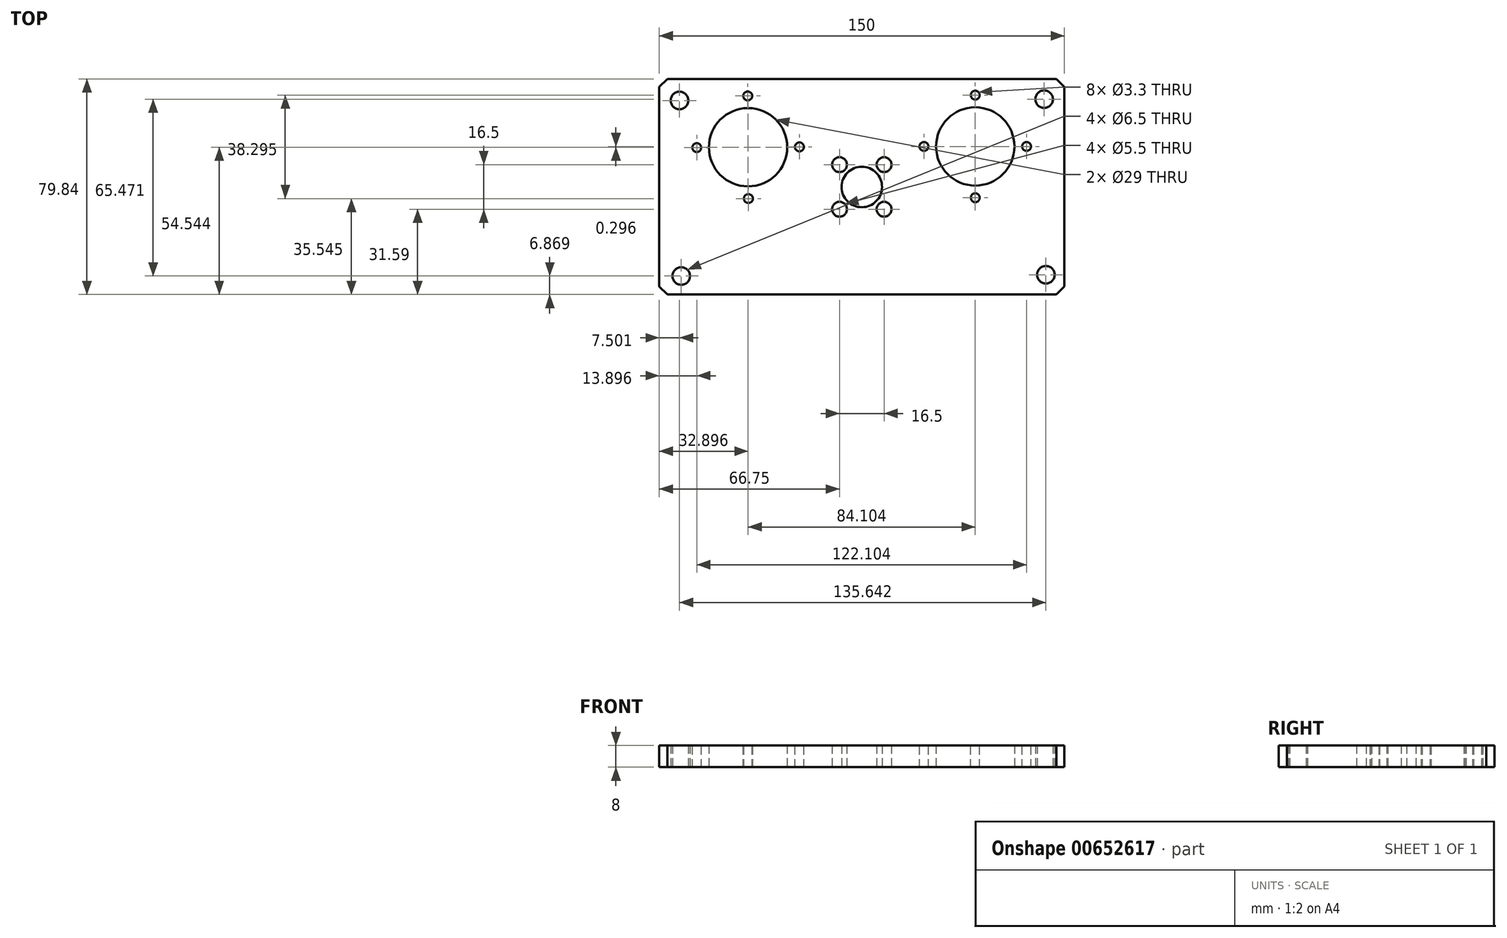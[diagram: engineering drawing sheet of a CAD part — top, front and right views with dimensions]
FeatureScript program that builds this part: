
annotation { "Feature Type Name" : "Feature", "Feature Type Description" : "" }
export const myFeature = defineFeature(function(context is Context, id is Id, definition is map)
    precondition{}
    {
        {
            var Q0;
            Q0=qCreatedBy(makeId("Top.planeOp"),FACE);
            var sketch = newSketch(context, id + "F0", { "sketchPlane" : qUnion([Q0])});
            skLineSegment(sketch, "E0.bottom", {"start": v(-75, 40) * mm, "end": v(75, 40) * mm});
            skLineSegment(sketch, "E0.top", {"start": v(-75, -39.84) * mm, "end": v(75, -39.84) * mm});
            skLineSegment(sketch, "E0.left", {"start": v(-75, 40) * mm, "end": v(-75, -39.84) * mm});
            skLineSegment(sketch, "E0.right", {"start": v(75, 40) * mm, "end": v(75, -39.84) * mm});
            skCircle(sketch, "E1", {"center": v(67.5, 32.5) * mm, "radius": 3.25 * mm});
            skCircle(sketch, "E2.0.1.0", {"center": v(68.14, -32.5) * mm, "radius": 3.25 * mm});
            skCircle(sketch, "E2.1.0.0", {"center": v(-67.5, 32.03) * mm, "radius": 3.25 * mm});
            skCircle(sketch, "E2.1.1.0", {"center": v(-66.86, -32.97) * mm, "radius": 3.25 * mm});
            skLineSegment(sketch, "E2.direction1", {"start": v(67.5, 32.5) * mm, "end": v(-67.5, 32.03) * mm, "construction": true});
            skLineSegment(sketch, "E2.direction2", {"start": v(67.5, 32.5) * mm, "end": v(68.14, -32.5) * mm, "construction": true});
            skCircle(sketch, "E3", {"center": v(0, 0) * mm, "radius": 7.5 * mm});
            skLineSegment(sketch, "E4.bottom", {"start": v(-8.25, 8.25) * mm, "end": v(8.25, 8.25) * mm, "construction": true});
            skLineSegment(sketch, "E4.top", {"start": v(-8.25, -8.25) * mm, "end": v(8.25, -8.25) * mm, "construction": true});
            skLineSegment(sketch, "E4.left", {"start": v(-8.25, 8.25) * mm, "end": v(-8.25, -8.25) * mm, "construction": true});
            skLineSegment(sketch, "E4.right", {"start": v(8.25, 8.25) * mm, "end": v(8.25, -8.25) * mm, "construction": true});
            skCircle(sketch, "E5", {"center": v(-8.25, 8.25) * mm, "radius": 2.75 * mm});
            skCircle(sketch, "E6.1.0", {"center": v(-8.25, -8.25) * mm, "radius": 2.75 * mm});
            skCircle(sketch, "E6.2.0", {"center": v(8.25, -8.25) * mm, "radius": 2.75 * mm});
            skCircle(sketch, "E6.3.0", {"center": v(8.25, 8.25) * mm, "radius": 2.75 * mm});
            skCircle(sketch, "E7", {"center": v(42, 15) * mm, "radius": 14.5 * mm});
            skCircle(sketch, "E8", {"center": v(23, 15) * mm, "radius": 1 * mm});
            skLineSegment(sketch, "E9", {"start": v(42, 15) * mm, "end": v(23, 15) * mm, "construction": true});
            skCircle(sketch, "E10.1.0", {"center": v(42, -4) * mm, "radius": 1 * mm});
            skCircle(sketch, "E10.2.0", {"center": v(61, 15) * mm, "radius": 1 * mm});
            skCircle(sketch, "E10.3.0", {"center": v(42, 34) * mm, "radius": 1 * mm});
            skLineSegment(sketch, "E11", {"start": v(0, 0) * mm, "end": v(-0.19, 53.35) * mm, "construction": true});
            skCircle(sketch, "E12.MirrorC", {"center": v(-42.1, 14.7) * mm, "radius": 14.5 * mm});
            skCircle(sketch, "E13.MirrorC", {"center": v(-42.24, 33.7) * mm, "radius": 1 * mm});
            skCircle(sketch, "E14.MirrorC", {"center": v(-23.1, 14.84) * mm, "radius": 1 * mm});
            skCircle(sketch, "E15.MirrorC", {"center": v(-41.97, -4.3) * mm, "radius": 1 * mm});
            skCircle(sketch, "E16.MirrorC", {"center": v(-61.1, 14.57) * mm, "radius": 1 * mm});
            skLineSegment(sketch, "E17.MirrorCS", {"start": v(-42.1, 14.7) * mm, "end": v(-23.1, 14.84) * mm, "construction": true});
            skSolve(sketch);
        }
        {
            var Q0;
            Q0 = qSketchRegion(id + "F0", true);
            extrude(context, id + "F1", {"entities" : qUnion([Q0]), "depth" : 8 * mm, "offsetDistance" : 25 * mm});
        }
        {
            var Q0;
            Q0=makeQuery(id+"F1.opExtrude","SWEPT_EDGE",EDGE,{"disambiguationData":[OSD([sQuery(id+"F0.wireOp",EDGE,"E0.top"),sQuery(id+"F0.wireOp",EDGE,"E0.right")])]});
            var Q1;
            Q1=makeQuery(id+"F1.opExtrude","SWEPT_EDGE",EDGE,{"disambiguationData":[OSD([sQuery(id+"F0.wireOp",EDGE,"E0.bottom"),sQuery(id+"F0.wireOp",EDGE,"E0.right")])]});
            var Q2;
            Q2=makeQuery(id+"F1.opExtrude","SWEPT_EDGE",EDGE,{"disambiguationData":[OSD([sQuery(id+"F0.wireOp",EDGE,"E0.top"),sQuery(id+"F0.wireOp",EDGE,"E0.left")])]});
            var Q3;
            Q3=makeQuery(id+"F1.opExtrude","SWEPT_EDGE",EDGE,{"disambiguationData":[OSD([sQuery(id+"F0.wireOp",EDGE,"E0.bottom"),sQuery(id+"F0.wireOp",EDGE,"E0.left")])]});
            chamfer(context, id + "F2", {"entities" : qUnion([Q0, Q1, Q2, Q3]), "width" : 3 * mm, "tangentPropagation" : true});
        }
        {
            var Q0;
            Q0=makeQuery(id+"F1.opExtrude","CAP_FACE",FACE,{"disambiguationData":[OSD([sQuery(id+"F0.wireOp",EDGE,"E0.bottom"),sQuery(id+"F0.wireOp",EDGE,"E0.top"),sQuery(id+"F0.wireOp",EDGE,"E0.left"),sQuery(id+"F0.wireOp",EDGE,"E0.right"),sQuery(id+"F0.wireOp",EDGE,"E1"),sQuery(id+"F0.wireOp",EDGE,"E2.0.1.0"),sQuery(id+"F0.wireOp",EDGE,"E2.1.0.0"),sQuery(id+"F0.wireOp",EDGE,"E2.1.1.0"),sQuery(id+"F0.wireOp",EDGE,"E3"),sQuery(id+"F0.wireOp",EDGE,"E5"),sQuery(id+"F0.wireOp",EDGE,"E6.1.0"),sQuery(id+"F0.wireOp",EDGE,"E6.2.0"),sQuery(id+"F0.wireOp",EDGE,"E6.3.0"),sQuery(id+"F0.wireOp",EDGE,"E7"),sQuery(id+"F0.wireOp",EDGE,"E8"),sQuery(id+"F0.wireOp",EDGE,"E10.1.0"),sQuery(id+"F0.wireOp",EDGE,"E10.2.0"),sQuery(id+"F0.wireOp",EDGE,"E10.3.0"),sQuery(id+"F0.wireOp",EDGE,"E12.MirrorC"),sQuery(id+"F0.wireOp",EDGE,"E13.MirrorC"),sQuery(id+"F0.wireOp",EDGE,"E14.MirrorC"),sQuery(id+"F0.wireOp",EDGE,"E15.MirrorC"),sQuery(id+"F0.wireOp",EDGE,"E16.MirrorC")])],"isStart":false});
            var sketch = newSketch(context, id + "F3", { "sketchPlane" : qUnion([Q0])});
            skCircle(sketch, "E18", {"center": v(-42.24, 33.7) * mm, "radius": 1.42 * mm});
            skCircle(sketch, "E19", {"center": v(-61.1, 14.57) * mm, "radius": 1.32 * mm});
            skCircle(sketch, "E20", {"center": v(-23.1, 14.84) * mm, "radius": 1.48 * mm});
            skCircle(sketch, "E21", {"center": v(-41.97, -4.3) * mm, "radius": 1.49 * mm});
            skCircle(sketch, "E22", {"center": v(23, 15) * mm, "radius": 1.62 * mm});
            skCircle(sketch, "E23", {"center": v(42, 34) * mm, "radius": 1.5 * mm});
            skCircle(sketch, "E24", {"center": v(42, -4) * mm, "radius": 1.3 * mm});
            skCircle(sketch, "E25", {"center": v(61, 15) * mm, "radius": 1.37 * mm});
            skSolve(sketch);
        }
        {
            var Q0;
            Q0=sQuery(id+"F3.wireOp",VERTEX,"E23.center");
            var Q1;
            Q1=sQuery(id+"F3.wireOp",VERTEX,"E25.center");
            var Q2;
            Q2=sQuery(id+"F3.wireOp",VERTEX,"E24.center");
            var Q3;
            Q3=sQuery(id+"F3.wireOp",VERTEX,"E22.center");
            var Q4;
            Q4=sQuery(id+"F3.wireOp",VERTEX,"E20.center");
            var Q5;
            Q5=sQuery(id+"F3.wireOp",VERTEX,"E18.center");
            var Q6;
            Q6=sQuery(id+"F3.wireOp",VERTEX,"E21.center");
            var Q7;
            Q7=sQuery(id+"F3.wireOp",VERTEX,"E19.center");
            var Q8;
            Q8=makeQuery(id+"F1.opExtrude","SWEPT_BODY",BODY,{"disambiguationData":[OSD([sQuery(id+"F0.wireOp",EDGE,"E0.bottom"),sQuery(id+"F0.wireOp",EDGE,"E0.top"),sQuery(id+"F0.wireOp",EDGE,"E0.left"),sQuery(id+"F0.wireOp",EDGE,"E0.right"),sQuery(id+"F0.wireOp",EDGE,"E1"),sQuery(id+"F0.wireOp",EDGE,"E2.0.1.0"),sQuery(id+"F0.wireOp",EDGE,"E2.1.0.0"),sQuery(id+"F0.wireOp",EDGE,"E2.1.1.0"),sQuery(id+"F0.wireOp",EDGE,"E3"),sQuery(id+"F0.wireOp",EDGE,"E5"),sQuery(id+"F0.wireOp",EDGE,"E6.1.0"),sQuery(id+"F0.wireOp",EDGE,"E6.2.0"),sQuery(id+"F0.wireOp",EDGE,"E6.3.0"),sQuery(id+"F0.wireOp",EDGE,"E7"),sQuery(id+"F0.wireOp",EDGE,"E8"),sQuery(id+"F0.wireOp",EDGE,"E10.1.0"),sQuery(id+"F0.wireOp",EDGE,"E10.2.0"),sQuery(id+"F0.wireOp",EDGE,"E10.3.0"),sQuery(id+"F0.wireOp",EDGE,"E12.MirrorC"),sQuery(id+"F0.wireOp",EDGE,"E13.MirrorC"),sQuery(id+"F0.wireOp",EDGE,"E14.MirrorC"),sQuery(id+"F0.wireOp",EDGE,"E15.MirrorC"),sQuery(id+"F0.wireOp",EDGE,"E16.MirrorC")])]});
            hole(context, id + "F4", {"style" : HoleStyle.SIMPLE, "endStyle" : HoleEndStyle.THROUGH, "standardTappedOrClearance" : lookupTablePath({ "standard" : "ISO", "engagement" : "75%", "pitch" : "0.7 mm", "size" : "M4", "type" : "Tapped" }), "standardBlindInLast" : lookupTablePath({ "standard" : "ISO", "engagement" : "75%", "pitch" : "0.7 mm", "size" : "M4", "type" : "Tapped" }), "holeDiameter" : 3.3 * mm, "majorDiameter" : 4 * mm, "showTappedDepth" : true, "isTappedThrough" : true, "tappedDepth" : 15 * mm, "tapClearance" : 3, "locations" : qUnion([Q0, Q1, Q2, Q3, Q4, Q5, Q6, Q7]), "scope" : qUnion([Q8])});
        }
    });
